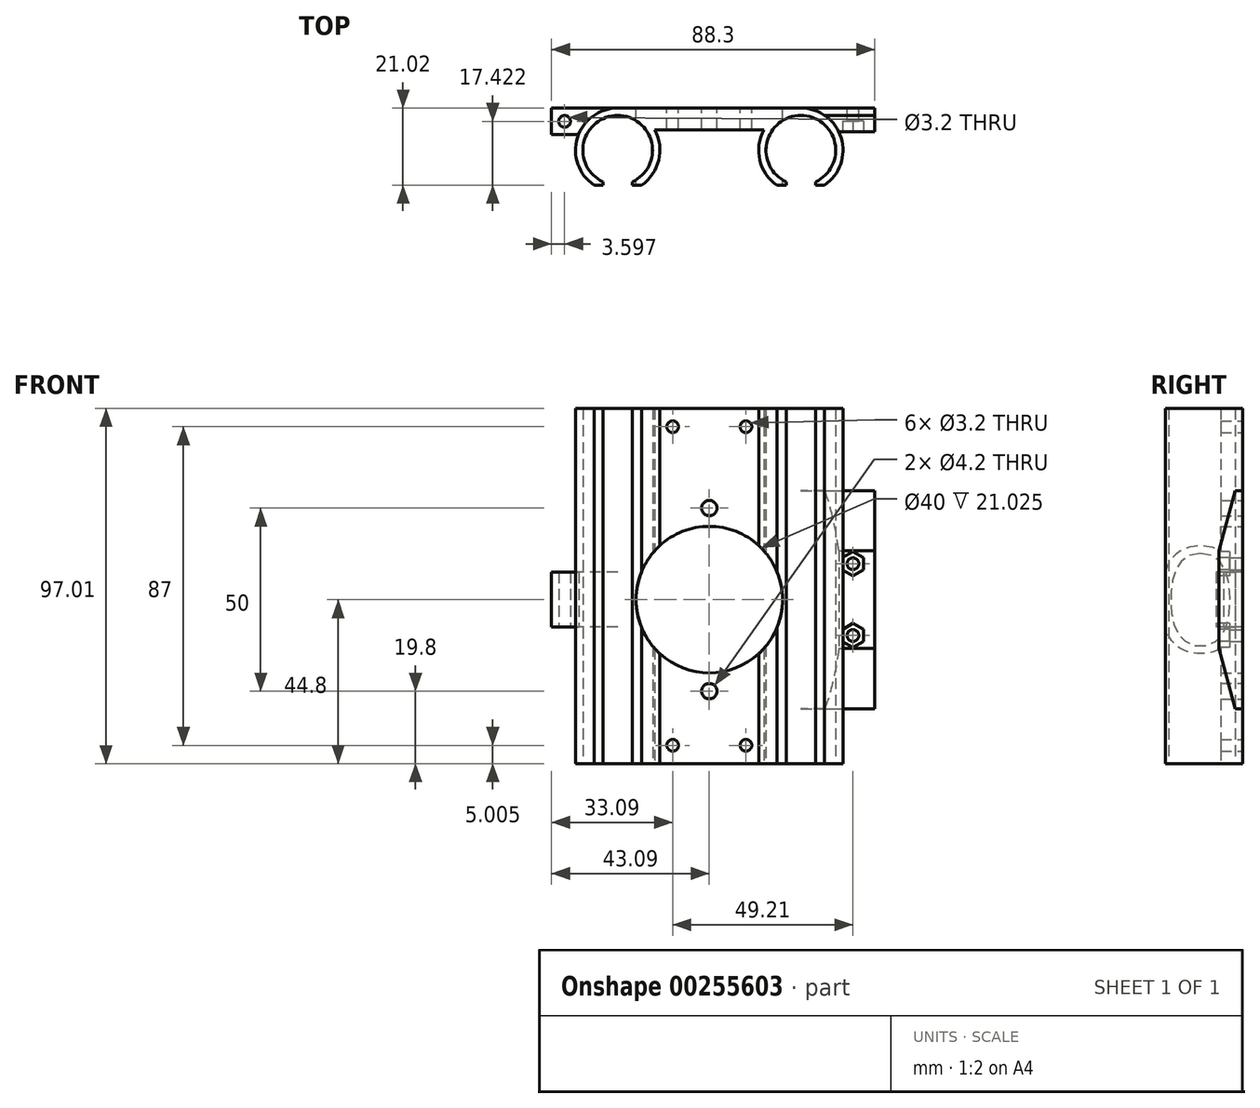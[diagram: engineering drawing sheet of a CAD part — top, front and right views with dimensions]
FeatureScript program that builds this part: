
annotation { "Feature Type Name" : "Feature", "Feature Type Description" : "" }
export const myFeature = defineFeature(function(context is Context, id is Id, definition is map)
    precondition{}
    {
        {
            var Q0;
            Q0=qCreatedBy(makeId("Top.planeOp"),FACE);
            var sketch = newSketch(context, id + "F0", { "sketchPlane" : qUnion([Q0])});
            skArc(sketch, "E0", {"start": v(-21, -8.63) * mm, "mid": v(-25, 9.51) * mm, "end": v(-29, -8.63) * mm});
            skArc(sketch, "E1.MirrorC", {"start": v(21, -8.63) * mm, "mid": v(25, 9.51) * mm, "end": v(29, -8.63) * mm});
            skArc(sketch, "E2", {"start": v(-25, 11.51) * mm, "mid": v(-36, 3.4) * mm, "end": v(-31.48, -9.51) * mm});
            skArc(sketch, "E3", {"start": v(14.9, 5.51) * mm, "mid": v(13.8, -2.7) * mm, "end": v(18.52, -9.51) * mm});
            skLineSegment(sketch, "E4", {"start": v(-25, 11.51) * mm, "end": v(25, 11.51) * mm});
            skLineSegment(sketch, "E5", {"start": v(-14.9, 5.51) * mm, "end": v(14.9, 5.51) * mm});
            skLineSegment(sketch, "E6", {"start": v(-31.48, -9.51) * mm, "end": v(-29, -9.51) * mm});
            skLineSegment(sketch, "E7", {"start": v(-29, -9.51) * mm, "end": v(-29, -8.63) * mm});
            skLineSegment(sketch, "E8", {"start": v(-21, -9.51) * mm, "end": v(-21, -8.63) * mm});
            skLineSegment(sketch, "E9", {"start": v(-25, 0) * mm, "end": v(-25, -16.58) * mm, "construction": true});
            skArc(sketch, "E10.trimOffspring", {"start": v(-18.52, -9.51) * mm, "mid": v(-13.8, -2.7) * mm, "end": v(-14.9, 5.51) * mm});
            skLineSegment(sketch, "E11.trimOffspring", {"start": v(-21, -9.51) * mm, "end": v(-18.52, -9.51) * mm});
            skLineSegment(sketch, "E12.MirrorCS", {"start": v(31.48, -9.51) * mm, "end": v(29, -9.51) * mm});
            skLineSegment(sketch, "E13.MirrorCS", {"start": v(29, -9.51) * mm, "end": v(29, -8.63) * mm});
            skLineSegment(sketch, "E14.MirrorCS", {"start": v(21, -9.51) * mm, "end": v(18.52, -9.51) * mm});
            skLineSegment(sketch, "E15.MirrorCS", {"start": v(21, -9.51) * mm, "end": v(21, -8.63) * mm});
            skArc(sketch, "E16.trimOffspring", {"start": v(31.48, -9.51) * mm, "mid": v(36, 3.4) * mm, "end": v(25, 11.51) * mm});
            skSolve(sketch);
        }
        {
            var Q0;
            Q0=makeQuery(id+"F0.imprint","IMPRINT",FACE,{"disambiguationData":[TD([[makeQuery(id+"F0.imprint","IMPRINT",EDGE,{"derivedFrom":sQuery(id+"F0.wireOp",EDGE,"E0")}),-1.0]])]});
            extrude(context, id + "F1", {"entities" : qUnion([Q0]), "endBound" : BoundingType.SYMMETRIC, "depth" : 80 * mm});
        }
        {
            var Q0;
            Q0=makeQuery(id+"F1.opExtrude","SWEPT_FACE",FACE,{"disambiguationData":[OSD([sQuery(id+"F0.wireOp",EDGE,"E4")])]});
            var sketch = newSketch(context, id + "F2", { "sketchPlane" : qUnion([Q0])});
            skCircle(sketch, "E17", {"center": v(0, 0) * mm, "radius": 20 * mm});
            skSolve(sketch);
        }
        {
            var Q0;
            Q0=makeQuery(id+"F2.imprint","IMPRINT",FACE,{"disambiguationData":[TD([[makeQuery(id+"F2.imprint","IMPRINT",EDGE,{"derivedFrom":sQuery(id+"F2.wireOp",EDGE,"E17")}),1.0]])]});
            var Q1;
            Q1=makeQuery(id+"F1.opExtrude","SWEPT_FACE",FACE,{"disambiguationData":[OSD([sQuery(id+"F0.wireOp",EDGE,"E5")])]});
            extrude(context, id + "F3", {"entities" : qUnion([Q0]), "operationType" : NewBodyOperationType.REMOVE, "endBound" : BoundingType.THROUGH_ALL, "oppositeDirection" : true, "endBoundEntityFace" : qUnion([Q1]), "depth" : 25 * mm});
        }
        {
            var Q0;
            Q0=qCreatedBy(makeId("Top.planeOp"),FACE);
            var sketch = newSketch(context, id + "F4", { "sketchPlane" : qUnion([Q0])});
            skLineSegment(sketch, "E18", {"start": v(25, 11.51) * mm, "end": v(45.2, 11.51) * mm});
            skLineSegment(sketch, "E19", {"start": v(45.2, 11.51) * mm, "end": v(45.2, 5.01) * mm});
            skLineSegment(sketch, "E20", {"start": v(45.2, 5.01) * mm, "end": v(35.36, 5.01) * mm});
            skArc(sketch, "E21.0", {"start": v(35.36, 5.01) * mm, "mid": v(31.12, 9.75) * mm, "end": v(25, 11.51) * mm});
            skPoint(sketch, "E22.orphan", {"position": v(31.48, -9.51) * mm});
            skLineSegment(sketch, "E23", {"start": v(39.2, 13.98) * mm, "end": v(39.2, -4.26) * mm, "construction": true});
            skSolve(sketch);
        }
        {
            var Q0;
            Q0 = qSketchRegion(id + "F4", true);
            extrude(context, id + "F5", {"entities" : qUnion([Q0]), "operationType" : NewBodyOperationType.ADD, "endBound" : BoundingType.SYMMETRIC, "depth" : 59.6 * mm});
        }
        {
            var Q0;
            Q0=makeQuery(id+"F5.boolean.opBoolean","MERGE",FACE,{"derivedFrom":[makeQuery(id+"F1.opExtrude","SWEPT_FACE",FACE,{"disambiguationData":[OSD([sQuery(id+"F0.wireOp",EDGE,"E4")])]}),makeQuery(id+"F5.opExtrude","SWEPT_FACE",FACE,{"disambiguationData":[OSD([sQuery(id+"F4.wireOp",EDGE,"E18")])]})]});
            var sketch = newSketch(context, id + "F6", { "sketchPlane" : qUnion([Q0])});
            skCircle(sketch, "E24", {"center": v(-39.2, -9.8) * mm, "radius": 1.6 * mm});
            skCircle(sketch, "E25.MirrorC", {"center": v(-39.2, 9.8) * mm, "radius": 1.6 * mm});
            skLineSegment(sketch, "E26", {"start": v(-25, -17.68) * mm, "end": v(-25, 16.28) * mm, "construction": true});
            skSolve(sketch);
        }
        {
            var Q0;
            Q0 = qSketchRegion(id + "F6", true);
            extrude(context, id + "F7", {"entities" : qUnion([Q0]), "operationType" : NewBodyOperationType.REMOVE, "endBound" : BoundingType.THROUGH_ALL, "oppositeDirection" : true, "depth" : 25 * mm});
        }
        {
            var Q0;
            Q0=makeQuery(id+"F5.opExtrude","SWEPT_FACE",FACE,{"disambiguationData":[OSD([sQuery(id+"F4.wireOp",EDGE,"E19")])]});
            var sketch = newSketch(context, id + "F8", { "sketchPlane" : qUnion([Q0])});
            skLineSegment(sketch, "E27", {"start": v(9.51, 29.8) * mm, "end": v(5.01, 13.37) * mm});
            skLineSegment(sketch, "E28.MirrorCS", {"start": v(9.51, -29.8) * mm, "end": v(5.01, -13.37) * mm});
            skLineSegment(sketch, "E29", {"start": v(9.51, 29.8) * mm, "end": v(5.01, 29.8) * mm});
            skLineSegment(sketch, "E30", {"start": v(5.01, 29.8) * mm, "end": v(5.01, 13.37) * mm});
            skLineSegment(sketch, "E31", {"start": v(5.01, -13.37) * mm, "end": v(5.01, -29.8) * mm});
            skLineSegment(sketch, "E32", {"start": v(5.01, -29.8) * mm, "end": v(9.51, -29.8) * mm});
            skSolve(sketch);
        }
        {
            var Q0;
            Q0=makeQuery(id+"F8.imprint","IMPRINT",FACE,{"disambiguationData":[TD([[makeQuery(id+"F8.imprint","IMPRINT",EDGE,{"derivedFrom":sQuery(id+"F8.wireOp",EDGE,"E27")}),-1.0]])]});
            var Q1;
            Q1=makeQuery(id+"F8.imprint","IMPRINT",FACE,{"disambiguationData":[TD([[makeQuery(id+"F8.imprint","IMPRINT",EDGE,{"derivedFrom":sQuery(id+"F8.wireOp",EDGE,"E28.MirrorCS")}),1.0]])]});
            var Q2;
            Q2=makeQuery(id+"F1.opExtrude","SWEPT_FACE",FACE,{"disambiguationData":[OSD([sQuery(id+"F0.wireOp",EDGE,"E16.trimOffspring")])]});
            extrude(context, id + "F9", {"entities" : qUnion([Q0, Q1]), "operationType" : NewBodyOperationType.REMOVE, "endBound" : BoundingType.UP_TO_SURFACE, "oppositeDirection" : true, "endBoundEntityFace" : qUnion([Q2]), "depth" : 25 * mm});
        }
        {
            var Q0;
            Q0=qCreatedBy(makeId("Top.planeOp"),FACE);
            var sketch = newSketch(context, id + "F10", { "sketchPlane" : qUnion([Q0])});
            skLineSegment(sketch, "E33", {"start": v(-25, 11.51) * mm, "end": v(-43.1, 11.51) * mm});
            skLineSegment(sketch, "E34", {"start": v(-43.1, 11.51) * mm, "end": v(-43.1, 4.31) * mm});
            skLineSegment(sketch, "E35", {"start": v(-43.1, 4.31) * mm, "end": v(-35.67, 4.31) * mm});
            skArc(sketch, "E36.0", {"start": v(-25, 11.51) * mm, "mid": v(-31.44, 9.54) * mm, "end": v(-35.67, 4.31) * mm});
            skCircle(sketch, "E37", {"center": v(-39.5, 7.91) * mm, "radius": 1.6 * mm});
            skLineSegment(sketch, "E38", {"start": v(-43.1, 7.91) * mm, "end": v(-33.36, 7.91) * mm, "construction": true});
            skCircle(sketch, "E39", {"center": v(-39.5, 7.91) * mm, "radius": 5 * mm, "construction": true});
            skSolve(sketch);
        }
        {
            var Q0;
            Q0 = qSketchRegion(id + "F10", true);
            extrude(context, id + "F11", {"entities" : qUnion([Q0]), "operationType" : NewBodyOperationType.ADD, "endBound" : BoundingType.SYMMETRIC, "depth" : 15 * mm});
        }
        {
            var Q0;
            Q0=makeQuery(id+"F11.boolean.opBoolean","MERGE",FACE,{"derivedFrom":[makeQuery(id+"F5.boolean.opBoolean","MERGE",FACE,{"derivedFrom":[makeQuery(id+"F1.opExtrude","SWEPT_FACE",FACE,{"disambiguationData":[OSD([sQuery(id+"F0.wireOp",EDGE,"E4")])]}),makeQuery(id+"F5.opExtrude","SWEPT_FACE",FACE,{"disambiguationData":[OSD([sQuery(id+"F4.wireOp",EDGE,"E18")])]})]}),makeQuery(id+"F11.opExtrude","SWEPT_FACE",FACE,{"disambiguationData":[OSD([sQuery(id+"F10.wireOp",EDGE,"E33")])]})]});
            var sketch = newSketch(context, id + "F12", { "sketchPlane" : qUnion([Q0])});
            skCircle(sketch, "E40", {"center": v(0, 25) * mm, "radius": 2.1 * mm});
            skCircle(sketch, "E41.MirrorC", {"center": v(0, -25) * mm, "radius": 2.1 * mm});
            skSolve(sketch);
        }
        {
            var Q0;
            Q0 = qSketchRegion(id + "F12", true);
            extrude(context, id + "F13", {"entities" : qUnion([Q0]), "operationType" : NewBodyOperationType.REMOVE, "endBound" : BoundingType.THROUGH_ALL, "oppositeDirection" : true, "depth" : 25 * mm});
        }
        {
            var Q0;
            Q0=makeQuery(id+"F1.opExtrude","CAP_FACE",FACE,{"disambiguationData":[OSD([sQuery(id+"F0.wireOp",EDGE,"E0"),sQuery(id+"F0.wireOp",EDGE,"E1.MirrorC"),sQuery(id+"F0.wireOp",EDGE,"E2"),sQuery(id+"F0.wireOp",EDGE,"E3"),sQuery(id+"F0.wireOp",EDGE,"E4"),sQuery(id+"F0.wireOp",EDGE,"E5"),sQuery(id+"F0.wireOp",EDGE,"E6"),sQuery(id+"F0.wireOp",EDGE,"E7"),sQuery(id+"F0.wireOp",EDGE,"E8"),sQuery(id+"F0.wireOp",EDGE,"E10.trimOffspring"),sQuery(id+"F0.wireOp",EDGE,"E11.trimOffspring"),sQuery(id+"F0.wireOp",EDGE,"E12.MirrorCS"),sQuery(id+"F0.wireOp",EDGE,"E13.MirrorCS"),sQuery(id+"F0.wireOp",EDGE,"E14.MirrorCS"),sQuery(id+"F0.wireOp",EDGE,"E15.MirrorCS"),sQuery(id+"F0.wireOp",EDGE,"E16.trimOffspring")])],"isStart":true});
            extrude(context, id + "F14", {"entities" : qUnion([Q0]), "operationType" : NewBodyOperationType.ADD, "depth" : (5 - .205) * mm});
        }
        {
            var Q0;
            Q0=makeQuery(id+"F1.opExtrude","CAP_FACE",FACE,{"disambiguationData":[OSD([sQuery(id+"F0.wireOp",EDGE,"E0"),sQuery(id+"F0.wireOp",EDGE,"E1.MirrorC"),sQuery(id+"F0.wireOp",EDGE,"E2"),sQuery(id+"F0.wireOp",EDGE,"E3"),sQuery(id+"F0.wireOp",EDGE,"E4"),sQuery(id+"F0.wireOp",EDGE,"E5"),sQuery(id+"F0.wireOp",EDGE,"E6"),sQuery(id+"F0.wireOp",EDGE,"E7"),sQuery(id+"F0.wireOp",EDGE,"E8"),sQuery(id+"F0.wireOp",EDGE,"E10.trimOffspring"),sQuery(id+"F0.wireOp",EDGE,"E11.trimOffspring"),sQuery(id+"F0.wireOp",EDGE,"E12.MirrorCS"),sQuery(id+"F0.wireOp",EDGE,"E13.MirrorCS"),sQuery(id+"F0.wireOp",EDGE,"E14.MirrorCS"),sQuery(id+"F0.wireOp",EDGE,"E15.MirrorCS"),sQuery(id+"F0.wireOp",EDGE,"E16.trimOffspring")])],"isStart":false});
            extrude(context, id + "F15", {"entities" : qUnion([Q0]), "operationType" : NewBodyOperationType.ADD, "depth" : 12.2 * mm});
        }
        {
            var Q0;
            Q0=makeQuery(id+"F5.boolean.opBoolean","MERGE",FACE,{"derivedFrom":[makeQuery(id+"F1.opExtrude","SWEPT_FACE",FACE,{"disambiguationData":[OSD([sQuery(id+"F0.wireOp",EDGE,"E4")])]}),makeQuery(id+"F5.opExtrude","SWEPT_FACE",FACE,{"disambiguationData":[OSD([sQuery(id+"F4.wireOp",EDGE,"E18")])]})]});
            var sketch = newSketch(context, id + "F16", { "sketchPlane" : qUnion([Q0])});
            skLineSegment(sketch, "E42.bottom", {"start": v(-10, 47.2) * mm, "end": v(10, 47.2) * mm, "construction": true});
            skLineSegment(sketch, "E42.top", {"start": v(-10, -39.8) * mm, "end": v(10, -39.8) * mm, "construction": true});
            skLineSegment(sketch, "E42.left", {"start": v(-10, 47.2) * mm, "end": v(-10, -39.8) * mm, "construction": true});
            skLineSegment(sketch, "E42.right", {"start": v(10, 47.2) * mm, "end": v(10, -39.8) * mm, "construction": true});
            skCircle(sketch, "E43", {"center": v(-10, 47.2) * mm, "radius": 1.6 * mm});
            skCircle(sketch, "E44", {"center": v(10, 47.2) * mm, "radius": 1.6 * mm});
            skCircle(sketch, "E45", {"center": v(-10, -39.8) * mm, "radius": 1.6 * mm});
            skCircle(sketch, "E46", {"center": v(10, -39.8) * mm, "radius": 1.6 * mm});
            skCircle(sketch, "E47", {"center": v(-10, 47.2) * mm, "radius": 4.93 * mm, "construction": true});
            skLineSegment(sketch, "E48.0", {"start": v(-14.9, 40) * mm, "end": v(-14.9, 0) * mm, "construction": true});
            skSolve(sketch);
        }
        {
            var Q0;
            Q0 = qSketchRegion(id + "F16", true);
            extrude(context, id + "F17", {"entities" : qUnion([Q0]), "operationType" : NewBodyOperationType.REMOVE, "endBound" : BoundingType.THROUGH_ALL, "oppositeDirection" : true, "depth" : 25 * mm});
        }
        {
            var Q0;
            Q0=makeQuery(id+"F5.opExtrude","SWEPT_FACE",FACE,{"disambiguationData":[OSD([sQuery(id+"F4.wireOp",EDGE,"E20")])]});
            var sketch = newSketch(context, id + "F18", { "sketchPlane" : qUnion([Q0])});
            skCircle(sketch, "E49.cCircle", {"center": v(39.2, 9.8) * mm, "radius": 2.85 * mm, "construction": true});
            skLineSegment(sketch, "E49.0", {"start": v(42.06, 8.15) * mm, "end": v(39.2, 6.5) * mm});
            skLineSegment(sketch, "E49.1", {"start": v(39.2, 6.5) * mm, "end": v(36.36, 8.15) * mm});
            skLineSegment(sketch, "E49.2", {"start": v(36.36, 8.15) * mm, "end": v(36.36, 11.45) * mm});
            skLineSegment(sketch, "E49.3", {"start": v(36.36, 11.45) * mm, "end": v(39.2, 13.1) * mm});
            skLineSegment(sketch, "E49.4", {"start": v(39.2, 13.1) * mm, "end": v(42.06, 11.45) * mm});
            skLineSegment(sketch, "E49.5", {"start": v(42.06, 11.45) * mm, "end": v(42.06, 8.15) * mm});
            skPoint(sketch, "E49.0.midPoint", {"position": v(40.63, 7.33) * mm});
            skCircle(sketch, "E50.cCircle", {"center": v(39.2, -9.8) * mm, "radius": 2.85 * mm, "construction": true});
            skLineSegment(sketch, "E50.0", {"start": v(42.06, -11.45) * mm, "end": v(39.2, -13.1) * mm});
            skLineSegment(sketch, "E50.1", {"start": v(39.2, -13.1) * mm, "end": v(36.36, -11.45) * mm});
            skLineSegment(sketch, "E50.2", {"start": v(36.36, -11.45) * mm, "end": v(36.36, -8.15) * mm});
            skLineSegment(sketch, "E50.3", {"start": v(36.36, -8.15) * mm, "end": v(39.2, -6.5) * mm});
            skLineSegment(sketch, "E50.4", {"start": v(39.2, -6.5) * mm, "end": v(42.06, -8.15) * mm});
            skLineSegment(sketch, "E50.5", {"start": v(42.06, -8.15) * mm, "end": v(42.06, -11.45) * mm});
            skPoint(sketch, "E50.0.midPoint", {"position": v(40.63, -12.27) * mm});
            skSolve(sketch);
        }
        {
            var Q0;
            Q0 = qSketchRegion(id + "F18", true);
            extrude(context, id + "F19", {"entities" : qUnion([Q0]), "operationType" : NewBodyOperationType.REMOVE, "oppositeDirection" : true, "depth" : 3 * mm});
        }
    });
